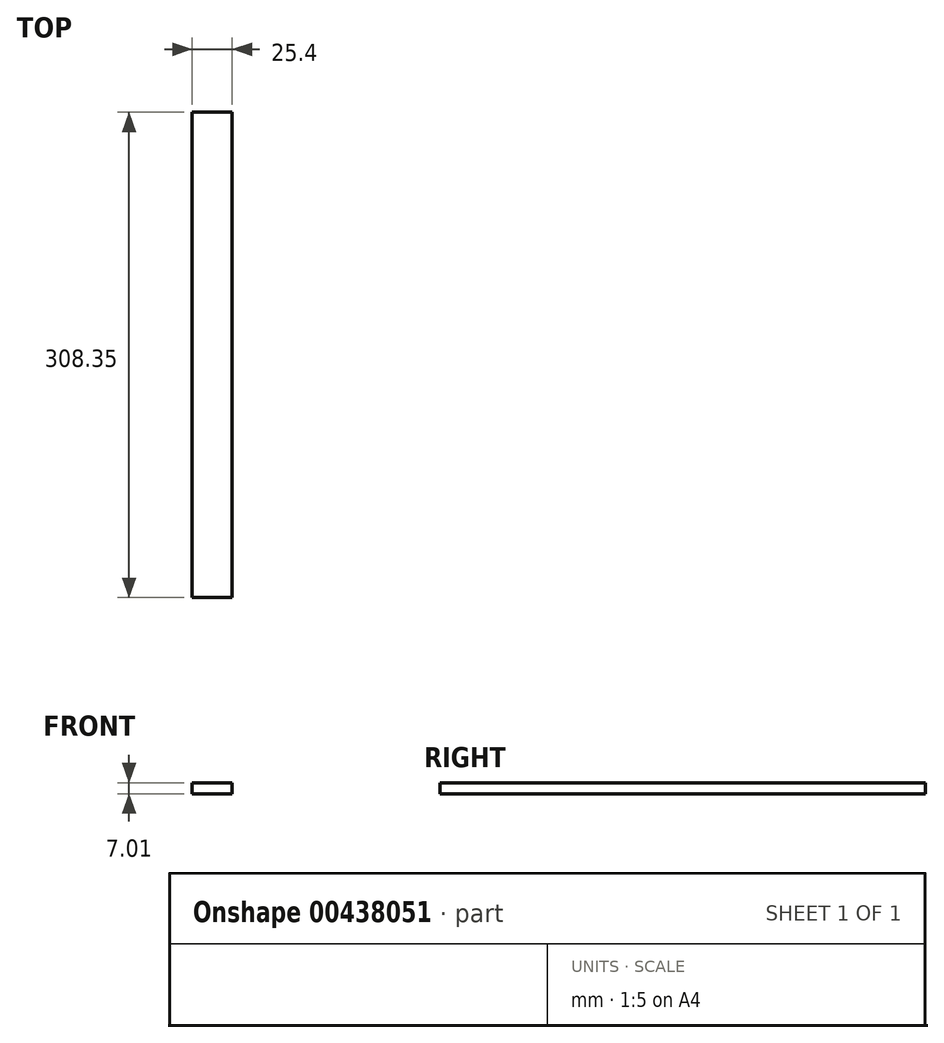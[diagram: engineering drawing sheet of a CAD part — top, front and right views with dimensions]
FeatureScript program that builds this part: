
annotation { "Feature Type Name" : "Feature", "Feature Type Description" : "" }
export const myFeature = defineFeature(function(context is Context, id is Id, definition is map)
    precondition{}
    {
        {
            var Q0;
            Q0=qCreatedBy(makeId("Right.planeOp"),FACE);
            var sketch = newSketch(context, id + "F0", { "sketchPlane" : qUnion([Q0])});
            skLineSegment(sketch, "E0.bottom", {"start": v(-154.28, 48.99) * mm, "end": v(154.07, 48.99) * mm});
            skLineSegment(sketch, "E0.top", {"start": v(-154.28, 41.98) * mm, "end": v(154.07, 41.98) * mm});
            skLineSegment(sketch, "E0.left", {"start": v(-154.28, 48.99) * mm, "end": v(-154.28, 41.98) * mm});
            skLineSegment(sketch, "E0.right", {"start": v(154.07, 48.99) * mm, "end": v(154.07, 41.98) * mm});
            skSolve(sketch);
        }
        {
            var Q0;
            Q0 = qSketchRegion(id + "F0", true);
            extrude(context, id + "F1", {"entities" : qUnion([Q0]), "depth" : 25.4 * mm});
        }
    });
